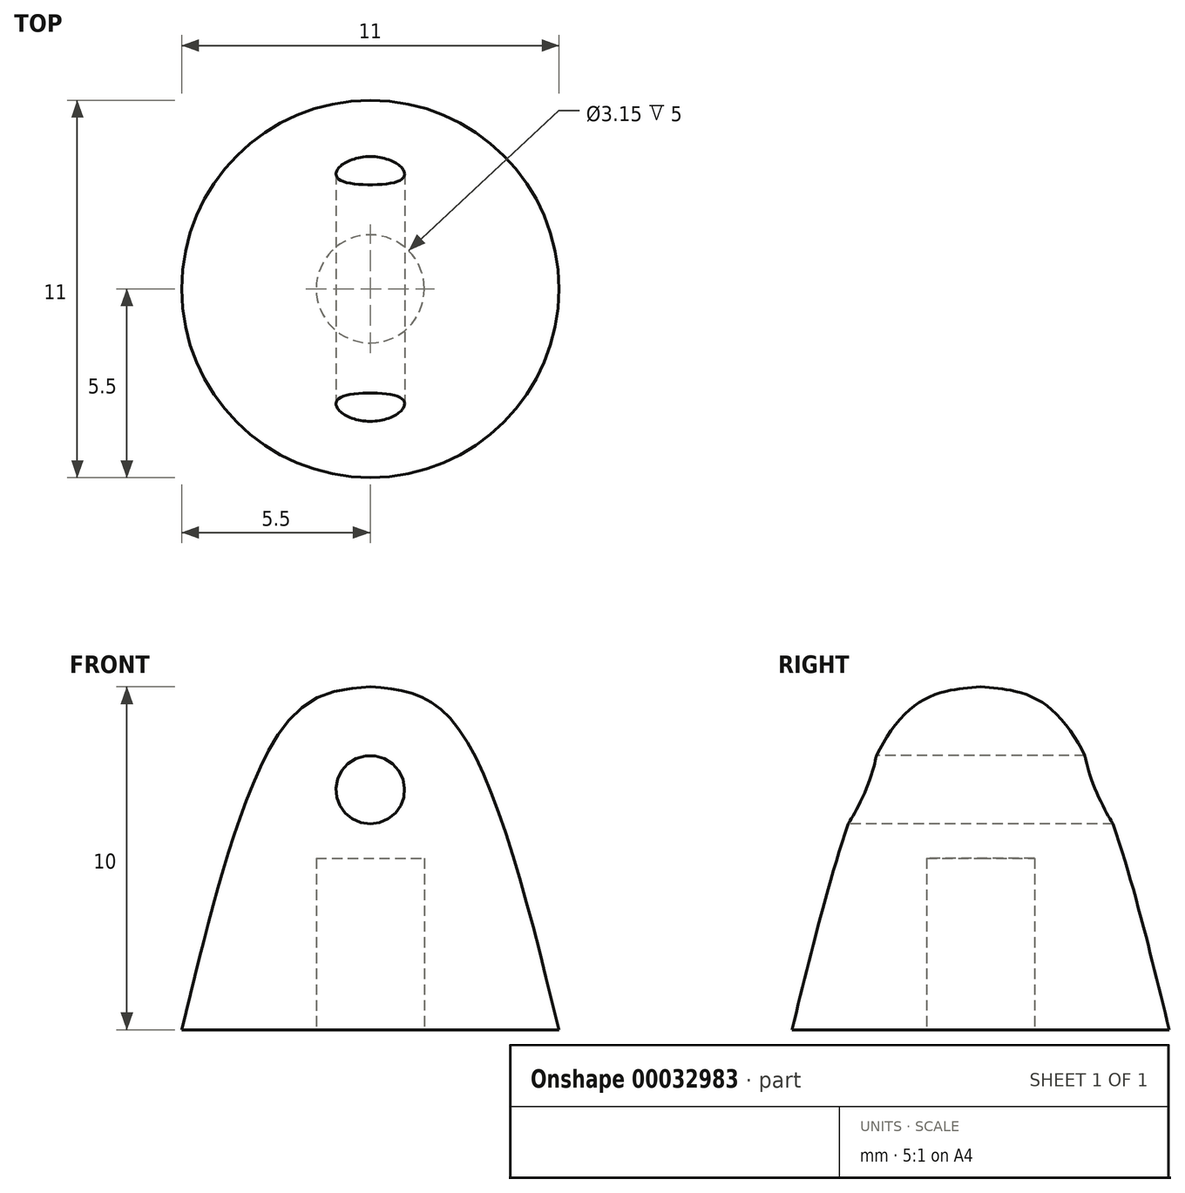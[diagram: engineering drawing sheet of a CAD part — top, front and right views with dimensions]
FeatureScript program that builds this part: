
annotation { "Feature Type Name" : "Feature", "Feature Type Description" : "" }
export const myFeature = defineFeature(function(context is Context, id is Id, definition is map)
    precondition{}
    {
        {
            var Q0;
            Q0=qCreatedBy(makeId("Front.planeOp"),FACE);
            var sketch = newSketch(context, id + "F0", { "sketchPlane" : qUnion([Q0])});
            skLineSegment(sketch, "E0.bottom", {"start": v(1.57, 0) * mm, "end": v(5.5, 0) * mm});
            skLineSegment(sketch, "E0.left", {"start": v(0, 5) * mm, "end": v(0, 10) * mm});
            skFitSpline(sketch, "E1", {"points": [v(0, 10) * mm, v(2.21, 9.2) * mm, v(5.5, 0) * mm], "startDerivative": vector(7.02, -0.55) * mm, "endDerivative": vector(4.3, -17.51) * mm});
            skLineSegment(sketch, "E2.top", {"start": v(0, 5) * mm, "end": v(1.57, 5) * mm});
            skLineSegment(sketch, "E2.right", {"start": v(1.57, 0) * mm, "end": v(1.57, 5) * mm});
            skSolve(sketch);
        }
        {
            var Q0;
            Q0=makeQuery(id+"F0.imprint","IMPRINT",FACE,{"disambiguationData":[TD([[makeQuery(id+"F0.imprint","IMPRINT",EDGE,{"derivedFrom":sQuery(id+"F0.wireOp",EDGE,"E0.bottom")}),1.0]])]});
            var Q1;
            Q1=sQuery(id+"F0.wireOp",EDGE,"E0.left");
            revolve(context, id + "F1", {"entities" : qUnion([Q0]), "axis" : qUnion([Q1]), "revolveType" : RevolveType.FULL});
        }
        {
            var Q0;
            Q0=qCreatedBy(makeId("Front.planeOp"),FACE);
            var sketch = newSketch(context, id + "F2", { "sketchPlane" : qUnion([Q0])});
            skCircle(sketch, "E3", {"center": v(0, 7) * mm, "radius": 1 * mm});
            skSolve(sketch);
        }
        {
            var Q0;
            Q0=qSketchRegion(id+"F2",true);
            extrude(context, id + "F3", {"entities" : qUnion([Q0]), "operationType" : NewBodyOperationType.REMOVE, "oppositeDirection" : true, "depth" : 10 * mm, "symmetric" : true});
        }
    });
